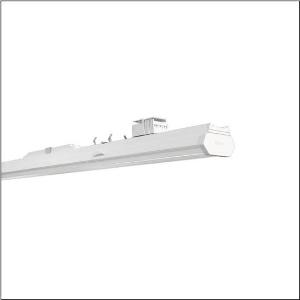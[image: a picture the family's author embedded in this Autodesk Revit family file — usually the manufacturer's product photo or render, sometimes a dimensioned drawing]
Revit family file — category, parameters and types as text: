
# Revit family: licross_11_protected_ho_51tp13cn4e5s
name_source: partatom
category: Lighting Fixtures
units: mm (PartAtom-declared; Revit-internal decimal feet)

## family parameters
Cut with Voids When Loaded = No
Host = Face
Light Source = No
Part Type = Normal
Room Calculation Point = No
Round Connector Dimension = Use Diameter
Shared = No

## types (1)
- --- (1 x LED, 14500 lm, 77.6 W, 4000K)
    Apparent Load = 78 VA
    CIE Flux Codes = 89 96 99 100 99
    Color Rendering = 80
    Color Temperature = 4000K
    Default Elevation = 1800 mm
    Description = Licross 11 Protected HO, luminaire insert, of sheet steel, galvanised, coil coated, white, length: 1.500mm, width: 90mm, height: 101mm, LED rated luminous flux: 14.500lm, light colour: 840, SDCM (Standard Deviation of Colour Matching)MacAdam ≤ 2 SDCM (initial), control gear: ON/OFF Multilumen, CLOi, with plug, 3-pole, with phase selection, mains connection: 220..240V, AC, 50/60Hz, start of lifetime: 78W, end of service life: 87W, internal wiring halogen-free, primary light control with lens, of plastic, primary optical cover: cover, of PMMA, light emission: direct distribution, primary light characteristic: symmetric, protection rating (complete): IP64, insulation class (complete): insulation class I (protective earthing), certification: CE, ENEC, VDE, UKCA, protection symbol: D if used in an environment with conductive dust loads with corresponding accessories, impact resistance: IK06, permissible ambient temperature for indoor applications: -35..+35°C, corresponds to IFS (International Featured Standards) requirements for safety and quality in the food industry, reducing of maximum allowable ambient temperature of 5°C with ceiling mounting, LABS conformity tested according to VDMA 24364:2018-05, The light source and the operating device comply with the requirements of the Ecodesign Regulation (EU) 2019/2020 and are replaceable in accordance with this regulation, packaging unit: 1 piece
    Height = 92 mm
    Lamp = 1 x LED
    Lamp Light Flux = 14500 lm
    Lamp Power = 77.6 W
    Lamp count = 1
    Length = 1500 mm
    Luminous efficacy = 187 lm/W
    Manufacturer = Siteco
    ModVariant = No
    Model = 51TP13CN4E5S
    Mounting Place = Ceiling
    Mounting Type = Pendant
    Number of Poles = 1
    OnlyDefault = Yes
    Power Factor = 1
    Product Name = Licross 11 Protected HO
    Product group = luminaire insert | ceiling pendant
    ProductGroupID = 901
    Protection Class = Protection class I
    Protection Degree = IP 64
    RLX_Detail_Level = 1
    RLX_Emergency_Light_Flux = 0 lm
    RLX_Emergency_Type = 0
    RLX_Emergency_Type_DB = No
    RlxData = <blob elided: 22397 chars, md5=32c06c64>
    Socket = socket
    Standby Power = 0 W
    System Light Flux = 14500 lm
    System Power = 78 W
    Type Comments = factory setting: luminous flux: 100 % | (A | C | E) | 181 mA
    Type Image = l_1256148.jpg
    URL = http://relux.com
    VarID = @adj_000633
    Voltage = 0 V
    Weight = 0.00 kg
    Width = 88 mm

## geometry (parser evidence)
native form markers: Blend x4, Sweep x10
no freeform markers — native parametric forms only
